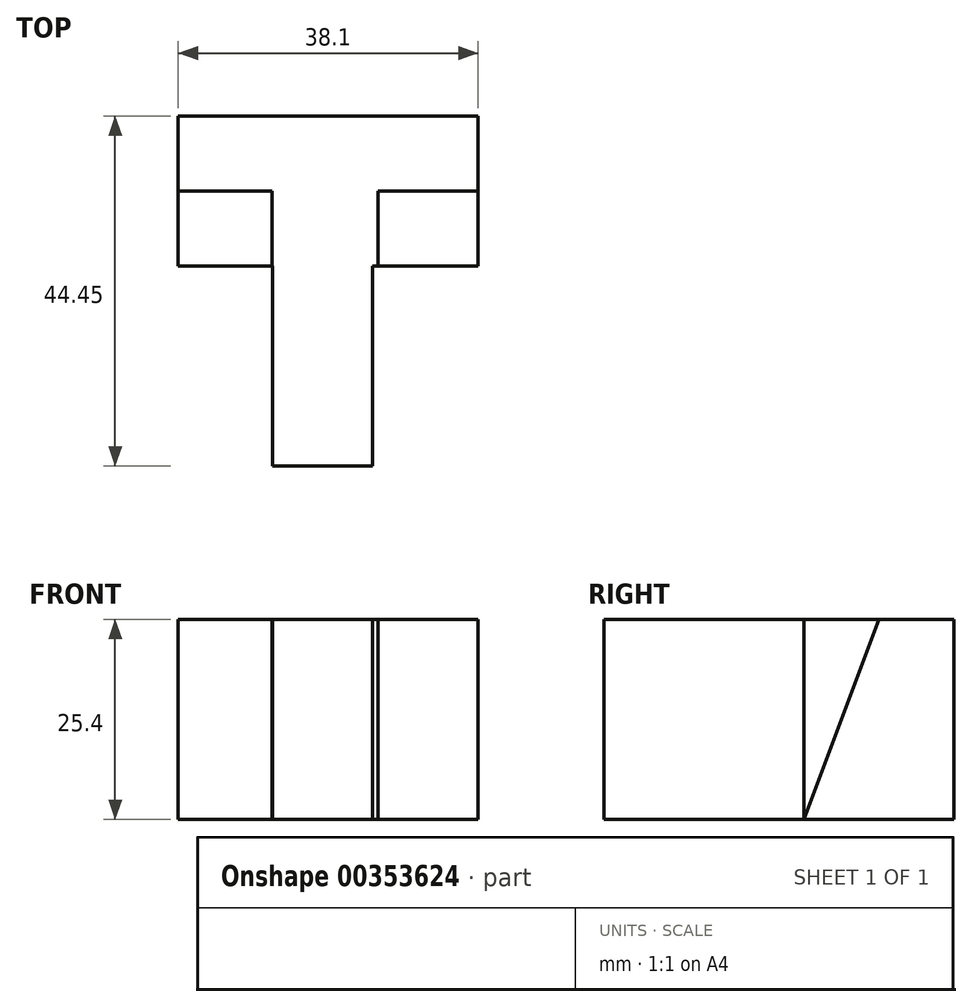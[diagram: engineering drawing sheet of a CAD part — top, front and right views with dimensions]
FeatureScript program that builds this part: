
annotation { "Feature Type Name" : "Feature", "Feature Type Description" : "" }
export const myFeature = defineFeature(function(context is Context, id is Id, definition is map)
    precondition{}
    {
        {
            var Q0;
            Q0=qCreatedBy(makeId("Top.planeOp"),FACE);
            var sketch = newSketch(context, id + "F0", { "sketchPlane" : qUnion([Q0])});
            skLineSegment(sketch, "E0", {"start": v(0, 0) * mm, "end": v(12.7, 0) * mm});
            skLineSegment(sketch, "E1", {"start": v(12.7, 0) * mm, "end": v(12.7, 25.4) * mm});
            skLineSegment(sketch, "E2", {"start": v(12.7, 25.4) * mm, "end": v(26.14, 25.4) * mm});
            skLineSegment(sketch, "E3", {"start": v(26.14, 25.4) * mm, "end": v(26.14, 44.45) * mm});
            skLineSegment(sketch, "E4", {"start": v(26.14, 44.45) * mm, "end": v(-11.96, 44.45) * mm});
            skLineSegment(sketch, "E5", {"start": v(-11.96, 44.45) * mm, "end": v(-11.96, 25.4) * mm});
            skLineSegment(sketch, "E6", {"start": v(-11.96, 25.4) * mm, "end": v(0, 25.4) * mm});
            skLineSegment(sketch, "E7", {"start": v(0, 25.4) * mm, "end": v(0, 0) * mm});
            skSolve(sketch);
        }
        {
            var Q0;
            Q0 = qSketchRegion(id + "F0", true);
            extrude(context, id + "F1", {"entities" : qUnion([Q0]), "depth" : 25.4 * mm});
        }
        {
            var Q0;
            Q0=makeQuery(id+"F1.opExtrude","SWEPT_FACE",FACE,{"disambiguationData":[OSD([sQuery(id+"F0.wireOp",EDGE,"E5")])]});
            var sketch = newSketch(context, id + "F2", { "sketchPlane" : qUnion([Q0])});
            skLineSegment(sketch, "E8", {"start": v(-25.4, 0) * mm, "end": v(-34.92, 25.4) * mm});
            skLineSegment(sketch, "E9", {"start": v(-34.92, 25.4) * mm, "end": v(-25.4, 25.4) * mm});
            skLineSegment(sketch, "E10", {"start": v(-25.4, 25.4) * mm, "end": v(-25.4, 0) * mm});
            skSolve(sketch);
        }
        {
            var Q0;
            Q0=makeQuery(id+"F2.imprint","IMPRINT",FACE,{"disambiguationData":[TD([[makeQuery(id+"F2.imprint","IMPRINT",EDGE,{"derivedFrom":sQuery(id+"F2.wireOp",EDGE,"E8")}),-1.0]])]});
            extrude(context, id + "F3", {"entities" : qUnion([Q0]), "operationType" : NewBodyOperationType.REMOVE, "oppositeDirection" : true, "depth" : 11.94 * mm});
        }
        {
            var Q0;
            Q0=makeQuery(id+"F1.opExtrude","SWEPT_FACE",FACE,{"disambiguationData":[OSD([sQuery(id+"F0.wireOp",EDGE,"E3")])]});
            var sketch = newSketch(context, id + "F4", { "sketchPlane" : qUnion([Q0])});
            skLineSegment(sketch, "E11", {"start": v(25.4, 0) * mm, "end": v(34.93, 25.4) * mm});
            skLineSegment(sketch, "E12", {"start": v(34.93, 25.4) * mm, "end": v(25.4, 25.4) * mm});
            skLineSegment(sketch, "E13", {"start": v(25.4, 25.4) * mm, "end": v(25.4, 0) * mm});
            skSolve(sketch);
        }
        {
            var Q0;
            Q0=makeQuery(id+"F4.imprint","IMPRINT",FACE,{"disambiguationData":[TD([[makeQuery(id+"F4.imprint","IMPRINT",EDGE,{"derivedFrom":sQuery(id+"F4.wireOp",EDGE,"E11")}),1.0]])]});
            extrude(context, id + "F5", {"entities" : qUnion([Q0]), "operationType" : NewBodyOperationType.REMOVE, "oppositeDirection" : true, "depth" : 12.7 * mm});
        }
    });
